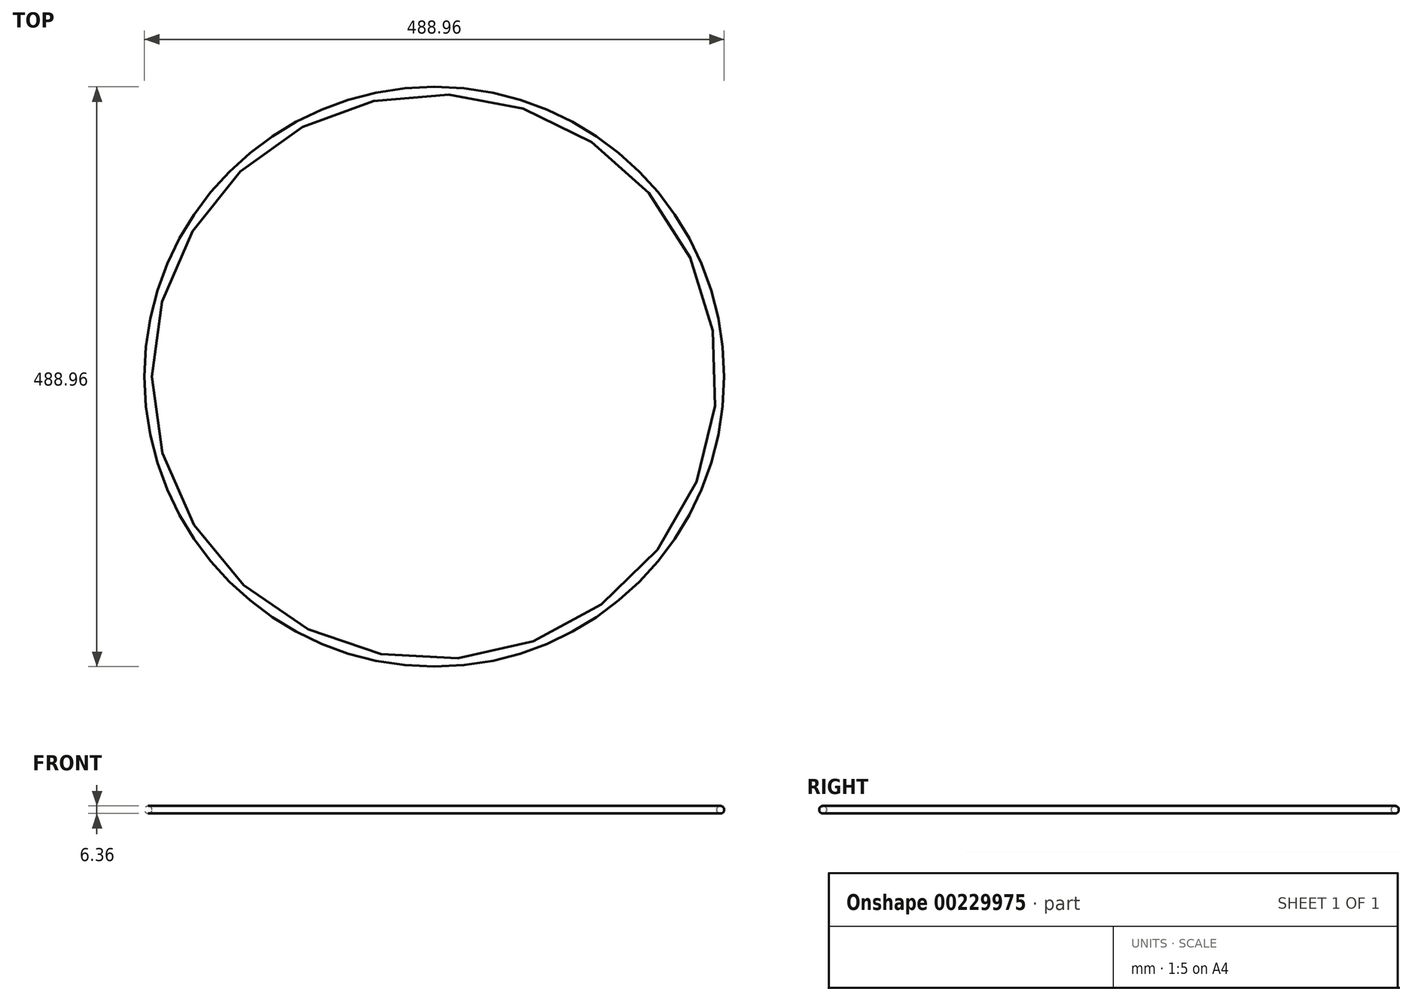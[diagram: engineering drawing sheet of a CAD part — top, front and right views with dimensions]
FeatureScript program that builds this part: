
annotation { "Feature Type Name" : "Feature", "Feature Type Description" : "" }
export const myFeature = defineFeature(function(context is Context, id is Id, definition is map)
    precondition{}
    {
        {
            var Q0;
            Q0=qCreatedBy(makeId("Front.planeOp"),FACE);
            var sketch = newSketch(context, id + "F0", { "sketchPlane" : qUnion([Q0])});
            skCircle(sketch, "E0", {"center": v(241.3, 0) * mm, "radius": 3.18 * mm});
            skLineSegment(sketch, "E1", {"start": v(0, 0) * mm, "end": v(0, 32.12) * mm, "construction": true});
            skSolve(sketch);
        }
        {
            var Q0;
            Q0 = qSketchRegion(id + "F0", true);
            var Q1;
            Q1=sQuery(id+"F0.wireOp",EDGE,"E1");
            revolve(context, id + "F1", {"entities" : qUnion([Q0]), "axis" : qUnion([Q1]), "revolveType" : RevolveType.FULL});
        }
    });
